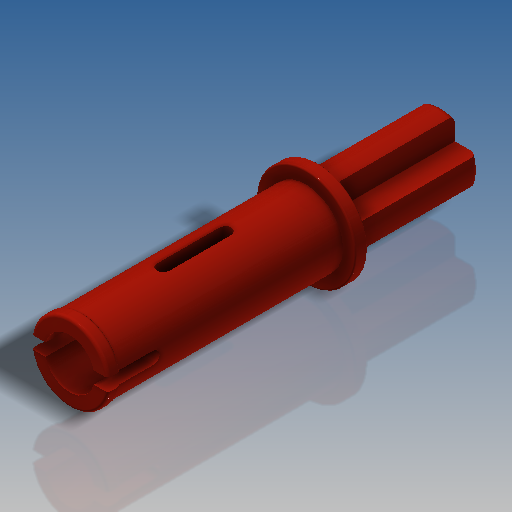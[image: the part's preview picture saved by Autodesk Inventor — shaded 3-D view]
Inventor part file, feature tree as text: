
AUTODESK INVENTOR PART (.ipt)
format: ipt  version: 2019.4 (Build 234330000, 330)  size: 334,336 bytes
history: native  units: mm (DEFAULTED — no unit token found)
features: sketch x3, extrude x3, revolve x1, fillet x1
ambient origin geometry x8: Origin, YZ Plane, XZ Plane, XY Plane, X Axis, Y Axis, Z Axis, Center Point
bodies: Body1 (feature_tree)
feature tree (8):
  sketch  "Sketch1"  dims[d1=4.8mm d2=5.0mm]
  revolve  "Revolution1"  [1 undecoded]
  extrude  "Extrusion1"  Depth=0.8mm
  extrude  "Extrusion2"  Depth=0.2mm
  extrude  "Extrusion4"  Depth=0.2mm
  fillet  "Fillet1"  Radius=0.8mm
  sketch  "Sketch2"  dims[d6=16.0mm d7=0.8mm]
  sketch  "Sketch4"  dims[d8=6.4mm d9=0.8mm d16=4.8mm d17=0.8mm d20=90.0deg d21=10.0mm d22=0.0mm d25=10.0mm d26=0.0mm d27=0.4mm d28=0.1mm d31=3.2mm d33=0.8mm d34=3.4mm d39=4.8mm d40=1.6mm d43=8.0mm d44=0.0mm d45=0.0mm d46=0.0mm d47=0.0mm d48=0.2mm]
note: 1 required parameter value undecoded (feature->parameter linkage not recoverable at this tier; creation-order binding heuristic only, values carry confidence <= 0.55)
